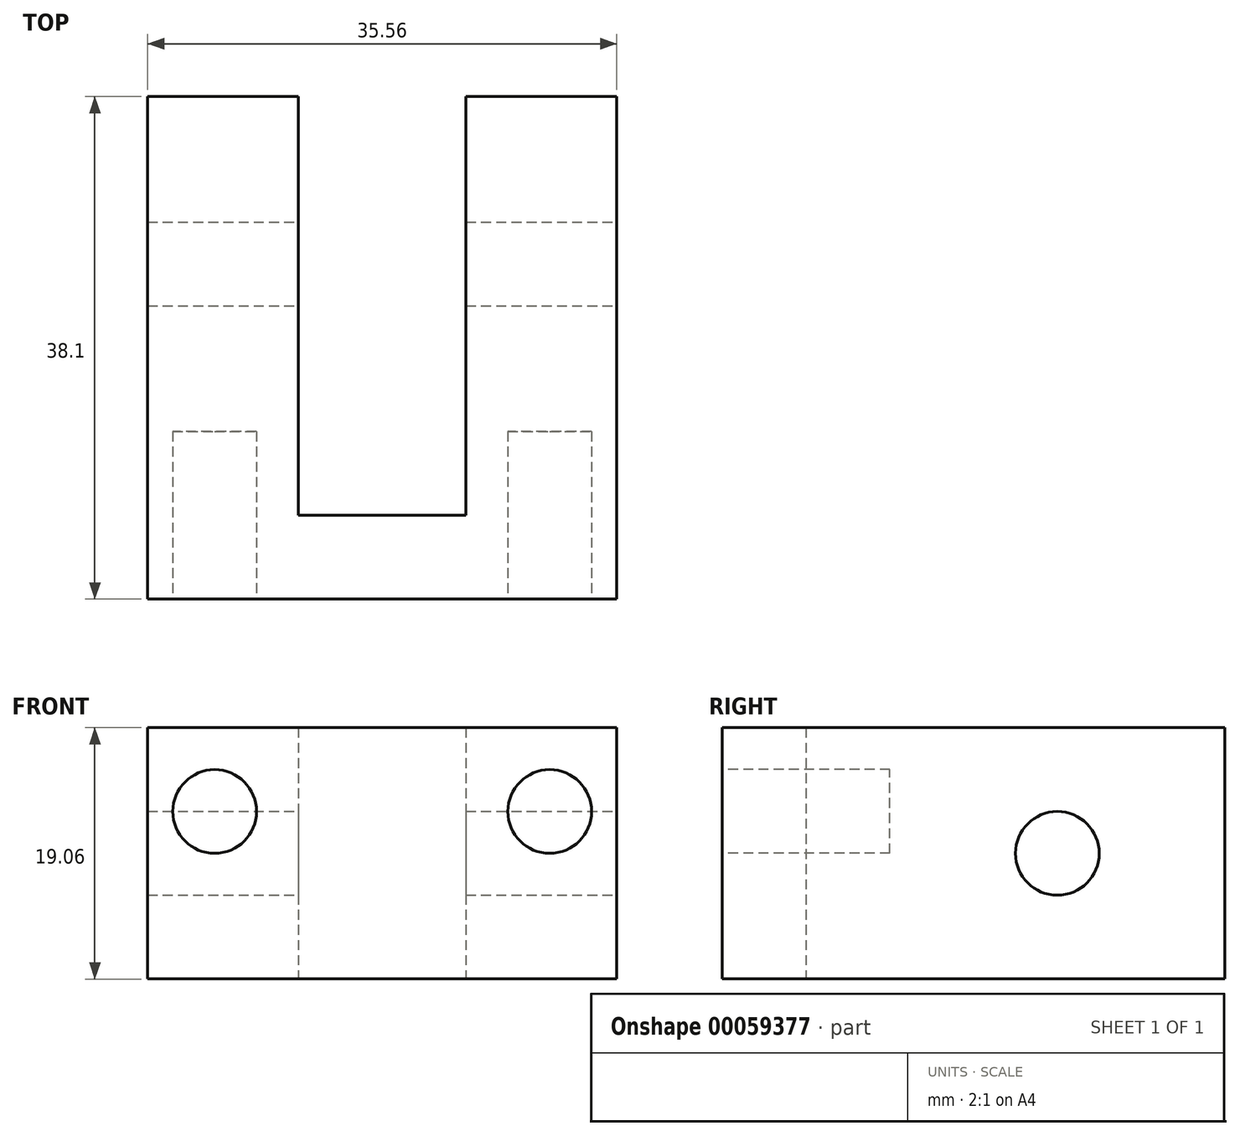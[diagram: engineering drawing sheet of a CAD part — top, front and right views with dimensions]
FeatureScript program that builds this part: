
annotation { "Feature Type Name" : "Feature", "Feature Type Description" : "" }
export const myFeature = defineFeature(function(context is Context, id is Id, definition is map)
    precondition{}
    {
        {
            var Q0;
            Q0=qCreatedBy(makeId("Top.planeOp"),FACE);
            var sketch = newSketch(context, id + "F0", { "sketchPlane" : qUnion([Q0])});
            skLineSegment(sketch, "E0", {"start": v(-6.35, 12.7) * mm, "end": v(-17.78, 12.7) * mm});
            skLineSegment(sketch, "E1", {"start": v(-17.78, 12.7) * mm, "end": v(-17.78, -25.4) * mm});
            skLineSegment(sketch, "E2", {"start": v(-17.78, -25.4) * mm, "end": v(0, -25.4) * mm});
            skLineSegment(sketch, "E3", {"start": v(6.35, -19.05) * mm, "end": v(-6.35, -19.05) * mm});
            skLineSegment(sketch, "E4", {"start": v(-6.35, -19.05) * mm, "end": v(-6.35, 12.7) * mm});
            skLineSegment(sketch, "E5.MirrorCS", {"start": v(6.35, -19.05) * mm, "end": v(6.35, 12.7) * mm});
            skLineSegment(sketch, "E6.MirrorCS", {"start": v(6.35, 12.7) * mm, "end": v(17.78, 12.7) * mm});
            skLineSegment(sketch, "E7.MirrorCS", {"start": v(17.78, 12.7) * mm, "end": v(17.78, -25.4) * mm});
            skLineSegment(sketch, "E8.MirrorCS", {"start": v(17.78, -25.4) * mm, "end": v(0, -25.4) * mm});
            skLineSegment(sketch, "E9", {"start": v(0, 0) * mm, "end": v(-23.2, 0) * mm});
            skLineSegment(sketch, "E10", {"start": v(0, 0) * mm, "end": v(0, 22.8) * mm});
            skSolve(sketch);
        }
        {
            var Q0;
            {var subQ0=sQuery(id+"F0.wireOp",EDGE,"E0");Q0=makeQuery(id+"F0.imprint","IMPRINT",FACE,{"disambiguationData":[TD([[makeQuery(id+"F0.imprint","IMPRINT",EDGE,{"derivedFrom":subQ0}),1.0]])]});}
            var Q1;
            {var subQ4=sQuery(id+"F0.wireOp",EDGE,"E2");Q1=makeQuery(id+"F0.imprint","IMPRINT",FACE,{"disambiguationData":[TD([[makeQuery(id+"F0.imprint","IMPRINT",EDGE,{"derivedFrom":subQ4}),1.0]])]});}
            extrude(context, id + "F1", {"entities" : qUnion([Q0, Q1]), "endBound" : BoundingType.SYMMETRIC, "depth" : 19.05 * mm});
        }
        {
            var Q0;
            Q0=makeQuery(id+"F1.opExtrude","SWEPT_FACE",FACE,{"disambiguationData":[OSD([sQuery(id+"F0.wireOp",EDGE,"E7.MirrorCS")])]});
            var sketch = newSketch(context, id + "F2", { "sketchPlane" : qUnion([Q0])});
            skCircle(sketch, "E11", {"center": v(0, 0) * mm, "radius": 3.18 * mm});
            skSolve(sketch);
        }
        {
            var Q0;
            Q0 = qSketchRegion(id + "F2", true);
            extrude(context, id + "F3", {"entities" : qUnion([Q0]), "operationType" : NewBodyOperationType.REMOVE, "oppositeDirection" : true, "depth" : 39.74 * mm});
        }
        {
            var Q0;
            Q0=makeQuery(id+"F1.opExtrude","SWEPT_FACE",FACE,{"disambiguationData":[OSD([sQuery(id+"F0.wireOp",EDGE,"E2"),sQuery(id+"F0.wireOp",EDGE,"E8.MirrorCS")])]});
            var sketch = newSketch(context, id + "F4", { "sketchPlane" : qUnion([Q0])});
            skCircle(sketch, "E12", {"center": v(-12.7, 3.17) * mm, "radius": 3.18 * mm});
            skCircle(sketch, "E13", {"center": v(12.7, 3.17) * mm, "radius": 3.18 * mm});
            skSolve(sketch);
        }
        {
            var Q0;
            Q0 = qSketchRegion(id + "F4", true);
            extrude(context, id + "F5", {"entities" : qUnion([Q0]), "operationType" : NewBodyOperationType.REMOVE, "oppositeDirection" : true, "depth" : 12.7 * mm});
        }
    });
